# Revit family: Faucet-Bath_Filler-KOHLER-Refinia-K-T97334_1
name_source: partatom
category: Plumbing Fixtures
revit_build: Autodesk Revit 2015 (Build: 20140606_1530(x64)
units: mm (PartAtom-declared; Revit-internal decimal feet)

## types (2) — shared parameters
ADA Compliant = No
Assembly Code = D2010
CW Connection = Yes
Cold Water Inlet = Cold Water Inlet
Date Modified = 03/11/2019
Default Elevation = 0"
Description = Floor-mount bath filler trim with handshower
Drain Included = No
Flow Rate = 7 GPM
HW Connection = Yes
Handle Clearance = 3 9/16"
Height = 32 5/8"
Hot Water Inlet = Hot Water Inlet
Length = 8 1/2"
Manufacturer = KOHLER Co.
MasterFormat 1995 = 15410
MasterFormat 2004 = 22.41.39
Material = Premium Metal Construction
Pressure = 45.00 psi
Product Documentation Link = https://www.us.kohler.com
Product Name = Refinia
Product Page URL = http://www.us.kohler.com
Spout Reach = 8 1/2"
URL = https://www.us.kohler.com
Vent Connection = No
Waste Connection = No
Waste Water Outlet = Waste Water Outlet
WaterSense Certified = Yes
Width = 9 13/16"

## per-type parameters (varying)
| type | Finish | Model | Type |
| CP-Polished Chrome | Kohler-Metal-CP-Polished_Chrome | K-T97334-4-CP | 1 |
| BN-Vibrant Brushed Nickel | Kohler-Metal-BN-Vibrant_Brushed_Nickel | K-T97334-4-BN | 2 |

## geometry (parser evidence)
native form markers: Sweep x4
no freeform markers — native parametric forms only
